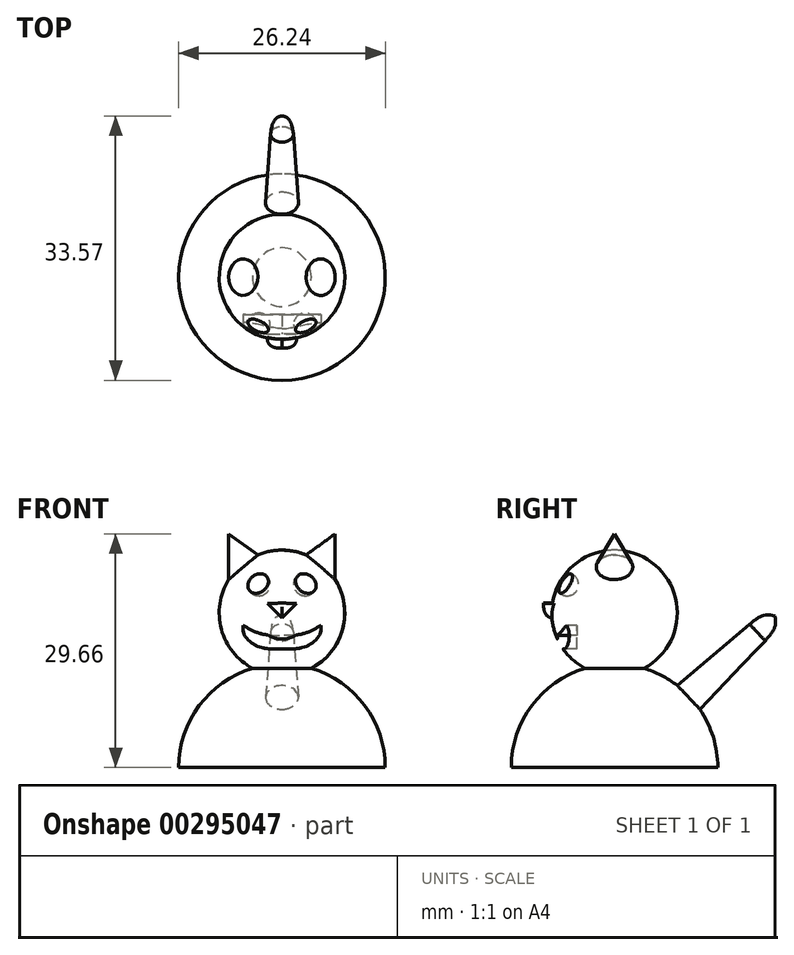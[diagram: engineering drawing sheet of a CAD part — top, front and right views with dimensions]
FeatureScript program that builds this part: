
annotation { "Feature Type Name" : "Feature", "Feature Type Description" : "" }
export const myFeature = defineFeature(function(context is Context, id is Id, definition is map)
    precondition{}
    {
        {
            var Q0;
            Q0=qCreatedBy(makeId("Top.planeOp"),FACE);
            var sketch = newSketch(context, id + "F0", { "sketchPlane" : qUnion([Q0])});
            skArc(sketch, "E0", {"start": v(0, 13.12) * mm, "mid": v(-13.12, 0) * mm, "end": v(0, -13.12) * mm});
            skLineSegment(sketch, "E1", {"start": v(0, 13.12) * mm, "end": v(0, -13.12) * mm});
            skSolve(sketch);
        }
        {
            var Q0;
            Q0=makeQuery(id+"F0.imprint","IMPRINT",FACE,{"disambiguationData":[TD([[makeQuery(id+"F0.imprint","IMPRINT",EDGE,{"derivedFrom":sQuery(id+"F0.wireOp",EDGE,"E0")}),1.0]])]});
            var Q1;
            Q1=sQuery(id+"F0.wireOp",EDGE,"E1");
            revolve(context, id + "F1", {"entities" : qUnion([Q0]), "axis" : qUnion([Q1]), "revolveType" : RevolveType.ONE_DIRECTION, "oppositeDirection" : true, "angle" : 180 * degree});
        }
        {
            var Q0;
            Q0=qCreatedBy(makeId("Front.planeOp"),FACE);
            var sketch = newSketch(context, id + "F2", { "sketchPlane" : qUnion([Q0])});
            skCircle(sketch, "E2", {"center": v(0, 19.62) * mm, "radius": 7.97 * mm});
            skLineSegment(sketch, "E3", {"start": v(0, 27.6) * mm, "end": v(0, 11.65) * mm});
            skSolve(sketch);
        }
        {
            var Q0;
            {var subQ0=sQuery(id+"F2.wireOp",EDGE,"E3");Q0=makeQuery(id+"F2.imprint","IMPRINT",FACE,{"disambiguationData":[TD([[makeQuery(id+"F2.imprint","IMPRINT",EDGE,{"derivedFrom":subQ0}),-1.0]])]});}
            var Q1;
            Q1=sQuery(id+"F2.wireOp",EDGE,"E3");
            revolve(context, id + "F3", {"operationType" : NewBodyOperationType.ADD, "entities" : qUnion([Q0]), "axis" : qUnion([Q1]), "revolveType" : RevolveType.FULL});
        }
        {
            var Q0;
            Q0=qCreatedBy(makeId("Front.planeOp"),FACE);
            var sketch = newSketch(context, id + "F4", { "sketchPlane" : qUnion([Q0])});
            skLineSegment(sketch, "E4", {"start": v(3.53, 23.33) * mm, "end": v(6.76, 22.87) * mm});
            skLineSegment(sketch, "E5", {"start": v(6.76, 29.66) * mm, "end": v(6.76, 22.87) * mm});
            skLineSegment(sketch, "E6", {"start": v(6.76, 29.66) * mm, "end": v(3.53, 23.33) * mm});
            skLineSegment(sketch, "E7.MirrorCS", {"start": v(-3.53, 23.33) * mm, "end": v(-6.76, 22.87) * mm});
            skLineSegment(sketch, "E8.MirrorCS", {"start": v(-6.76, 29.66) * mm, "end": v(-6.76, 22.87) * mm});
            skLineSegment(sketch, "E9.MirrorCS", {"start": v(-6.76, 29.66) * mm, "end": v(-3.53, 23.33) * mm});
            skSolve(sketch);
        }
        {
            var Q0;
            Q0=makeQuery(id+"F4.imprint","IMPRINT",FACE,{"disambiguationData":[TD([[makeQuery(id+"F4.imprint","IMPRINT",EDGE,{"derivedFrom":sQuery(id+"F4.wireOp",EDGE,"E4")}),1.0]])]});
            var Q1;
            Q1=sQuery(id+"F4.wireOp",EDGE,"E6");
            revolve(context, id + "F5", {"operationType" : NewBodyOperationType.ADD, "entities" : qUnion([Q0]), "axis" : qUnion([Q1]), "revolveType" : RevolveType.FULL});
        }
        {
            var Q0;
            Q0=makeQuery(id+"F4.imprint","IMPRINT",FACE,{"disambiguationData":[TD([[makeQuery(id+"F4.imprint","IMPRINT",EDGE,{"derivedFrom":sQuery(id+"F4.wireOp",EDGE,"E7.MirrorCS")}),-1.0]])]});
            var Q1;
            Q1=sQuery(id+"F4.wireOp",EDGE,"E9.MirrorCS");
            revolve(context, id + "F6", {"operationType" : NewBodyOperationType.ADD, "entities" : qUnion([Q0]), "axis" : qUnion([Q1]), "revolveType" : RevolveType.FULL});
        }
        {
            var Q0;
            Q0=qCreatedBy(makeId("Front.planeOp"),FACE);
            var sketch = newSketch(context, id + "F7", { "sketchPlane" : qUnion([Q0])});
            skLineSegment(sketch, "E10", {"start": v(0, 20.88) * mm, "end": v(0, 19.01) * mm});
            skLineSegment(sketch, "E11", {"start": v(0, 19.01) * mm, "end": v(-1.84, 20.8) * mm});
            skLineSegment(sketch, "E12", {"start": v(-1.84, 20.8) * mm, "end": v(0, 20.88) * mm});
            skLineSegment(sketch, "E13.MirrorCS", {"start": v(1.84, 20.8) * mm, "end": v(0, 20.88) * mm});
            skLineSegment(sketch, "E14.MirrorCS", {"start": v(0, 19.01) * mm, "end": v(1.84, 20.8) * mm});
            skSolve(sketch);
        }
        {
            var Q0;
            Q0 = qSketchRegion(id + "F7", true);
            extrude(context, id + "F8", {"entities" : qUnion([Q0]), "operationType" : NewBodyOperationType.ADD, "depth" : 9 * mm});
        }
        {
            var Q0;
            Q0=makeQuery(id+"F8.opExtrude","CAP_EDGE",EDGE,{"disambiguationData":[OSD([sQuery(id+"F7.wireOp",EDGE,"E11")])],"isStart":false});
            var Q1;
            Q1=makeQuery(id+"F8.opExtrude","CAP_EDGE",EDGE,{"disambiguationData":[OSD([sQuery(id+"F7.wireOp",EDGE,"E14.MirrorCS")])],"isStart":false});
            fillet(context, id + "F9", {"entities" : qUnion([Q0, Q1]), "radius" : 1 * mm, "tangentPropagation" : true, "allowEdgeOverflow" : false});
        }
        {
            var Q0;
            Q0=qCreatedBy(makeId("Front.planeOp"),FACE);
            cPlane(context, id + "F10", {"entities" : qUnion([Q0]), "cplaneType" : CPlaneType.OFFSET, "offset" : 6 * mm, "width" : 150 * mm, "height" : 150 * mm});
        }
        {
            var Q0;
            Q0=qCreatedBy(id+"F10.planeOp",FACE);
            var sketch = newSketch(context, id + "F11", { "sketchPlane" : qUnion([Q0])});
            skCircle(sketch, "E15", {"center": v(-2.93, 23.23) * mm, "radius": 1.44 * mm});
            skCircle(sketch, "E16.MirrorC", {"center": v(2.93, 23.23) * mm, "radius": 1.44 * mm});
            skLineSegment(sketch, "E17", {"start": v(-2.93, 23.23) * mm, "end": v(-2.93, 24.67) * mm});
            skLineSegment(sketch, "E18", {"start": v(2.93, 23.23) * mm, "end": v(2.93, 24.67) * mm});
            skLineSegment(sketch, "E19", {"start": v(-2.93, 23.23) * mm, "end": v(-2.93, 21.8) * mm});
            skLineSegment(sketch, "E20", {"start": v(2.93, 23.23) * mm, "end": v(2.93, 21.8) * mm});
            skSolve(sketch);
        }
        {
            var Q0;
            {var subQ0=sQuery(id+"F11.wireOp",EDGE,"E17");Q0=makeQuery(id+"F11.imprint","IMPRINT",FACE,{"disambiguationData":[TD([[makeQuery(id+"F11.imprint","IMPRINT",EDGE,{"derivedFrom":subQ0}),-1.0]])]});}
            var Q1;
            Q1=sQuery(id+"F11.wireOp",EDGE,"E17");
            revolve(context, id + "F12", {"operationType" : NewBodyOperationType.REMOVE, "entities" : qUnion([Q0]), "axis" : qUnion([Q1]), "revolveType" : RevolveType.FULL, "oppositeDirection" : true});
        }
        {
            var Q0;
            {var subQ0=sQuery(id+"F11.wireOp",EDGE,"E18");Q0=makeQuery(id+"F11.imprint","IMPRINT",FACE,{"disambiguationData":[TD([[makeQuery(id+"F11.imprint","IMPRINT",EDGE,{"derivedFrom":subQ0}),-1.0]])]});}
            var Q1;
            Q1=sQuery(id+"F11.wireOp",EDGE,"E18");
            revolve(context, id + "F13", {"operationType" : NewBodyOperationType.REMOVE, "entities" : qUnion([Q0]), "axis" : qUnion([Q1]), "revolveType" : RevolveType.FULL, "oppositeDirection" : true});
        }
        {
            var Q0;
            Q0=qCreatedBy(id+"F10.planeOp",FACE);
            var sketch = newSketch(context, id + "F14", { "sketchPlane" : qUnion([Q0])});
            skFitSpline(sketch, "E21", {"points": [v(0, 15.05) * mm, v(3.07, 15.38) * mm, v(4.82, 16.93) * mm, v(4.96, 18.03) * mm], "startDerivative": vector(7.96, -0.22) * mm, "endDerivative": vector(-0.26, 4.36) * mm});
            skFitSpline(sketch, "E22", {"points": [v(4.96, 18.03) * mm, v(2.7, 16.99) * mm, v(0, 16.74) * mm], "startDerivative": vector(-4.44, -2.54) * mm, "endDerivative": vector(-5.47, -0.05) * mm});
            skFitSpline(sketch, "E23.MirrorCS", {"points": [v(-4.96, 18.03) * mm, v(-2.7, 16.99) * mm, v(0, 16.74) * mm], "startDerivative": vector(4.44, -2.54) * mm, "endDerivative": vector(5.47, -0.05) * mm});
            skFitSpline(sketch, "E24.MirrorCS", {"points": [v(0, 15.05) * mm, v(-3.07, 15.38) * mm, v(-4.82, 16.93) * mm, v(-4.96, 18.03) * mm], "startDerivative": vector(-7.96, -0.22) * mm, "endDerivative": vector(0.26, 4.36) * mm});
            skSolve(sketch);
        }
        {
            var Q0;
            Q0 = qSketchRegion(id + "F14", true);
            extrude(context, id + "F15", {"entities" : qUnion([Q0]), "operationType" : NewBodyOperationType.REMOVE, "endBound" : BoundingType.SYMMETRIC, "oppositeDirection" : true, "depth" : 2.5 * mm});
        }
        {
            var Q0;
            Q0=qCreatedBy(makeId("Right.planeOp"),FACE);
            var sketch = newSketch(context, id + "F16", { "sketchPlane" : qUnion([Q0])});
            skLineSegment(sketch, "E25", {"start": v(0, 0) * mm, "end": v(20.37, 19.23) * mm});
            skFitSpline(sketch, "E26", {"points": [v(20.37, 19.23) * mm, v(20.37, 17.85) * mm, v(19.15, 16.09) * mm], "startDerivative": vector(0.5, -3.09) * mm, "endDerivative": vector(-2.82, -3.2) * mm});
            skLineSegment(sketch, "E27", {"start": v(19.15, 16.09) * mm, "end": v(3.8, 0) * mm});
            skLineSegment(sketch, "E28", {"start": v(3.8, 0) * mm, "end": v(0, 0) * mm});
            skSolve(sketch);
        }
        {
            var Q0;
            Q0=makeQuery(id+"F16.imprint","IMPRINT",FACE,{"disambiguationData":[TD([[makeQuery(id+"F16.imprint","IMPRINT",EDGE,{"derivedFrom":sQuery(id+"F16.wireOp",EDGE,"E25")}),-1.0]])]});
            var Q1;
            Q1=sQuery(id+"F16.wireOp",EDGE,"E25");
            revolve(context, id + "F17", {"operationType" : NewBodyOperationType.ADD, "entities" : qUnion([Q0]), "axis" : qUnion([Q1]), "revolveType" : RevolveType.FULL});
        }
    });
